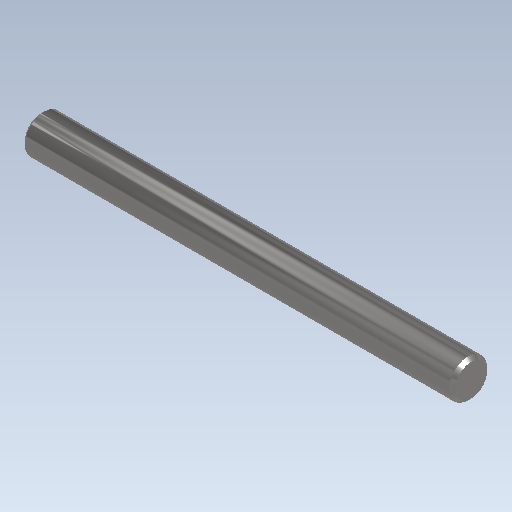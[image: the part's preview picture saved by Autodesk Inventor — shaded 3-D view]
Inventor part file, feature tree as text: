
AUTODESK INVENTOR PART (.ipt)
format: ipt  version: 2020 (Build 240168000, 168)  size: 101,376 bytes
history: native  units: mm
features: other x1, extrude x1, chamfer x1, sketch x1
ambient origin geometry x8: Origin, YZ Plane, XZ Plane, XY Plane, X Axis, Y Axis, Z Axis, Center Point
bodies: Body1 (feature_tree)
feature tree (4):
  other  "Твердое тело1"
  extrude  "Выдавливание1"  Depth=1.2mm
  chamfer  "Фаска1"  Distance=13.5mm
  sketch  "Эскиз1"
